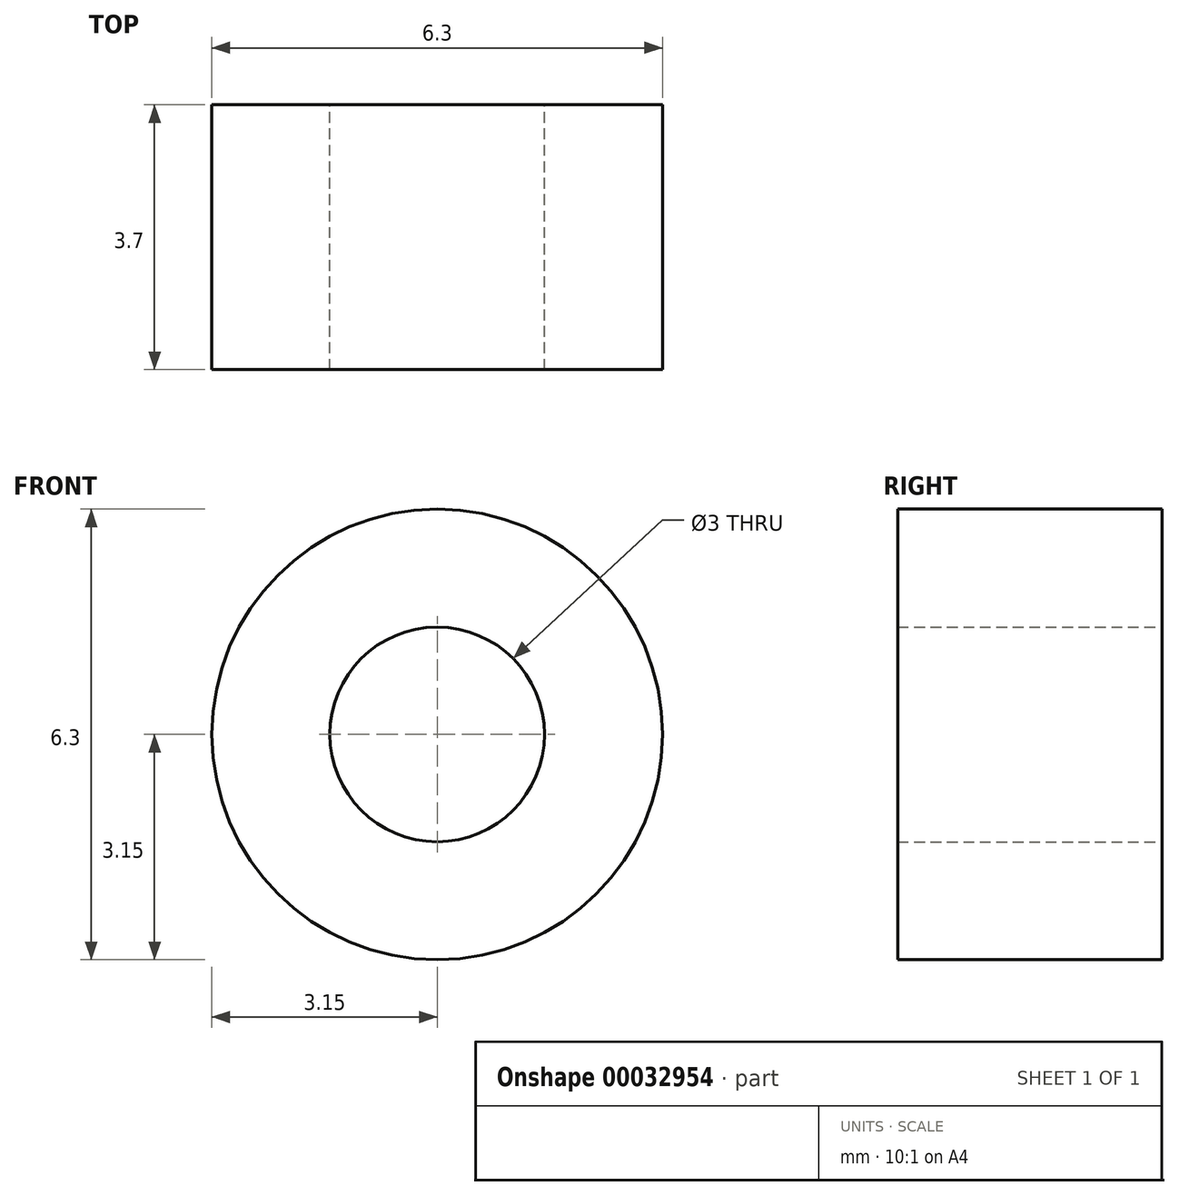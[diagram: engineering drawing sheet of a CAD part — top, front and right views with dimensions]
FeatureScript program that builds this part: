
annotation { "Feature Type Name" : "Feature", "Feature Type Description" : "" }
export const myFeature = defineFeature(function(context is Context, id is Id, definition is map)
    precondition{}
    {
        {
            var Q0;
            Q0=qCreatedBy(makeId("Front.planeOp"),FACE);
            var sketch = newSketch(context, id + "F0", { "sketchPlane" : qUnion([Q0])});
            skCircle(sketch, "E0", {"center": v(0, 0) * mm, "radius": 1.5 * mm});
            skCircle(sketch, "E1", {"center": v(0, 0) * mm, "radius": 3.15 * mm});
            skSolve(sketch);
        }
        {
            var Q0;
            Q0=qSketchRegion(id+"F0",true);
            extrude(context, id + "F1", {"entities" : qUnion([Q0]), "depth" : 3.7 * mm});
        }
    });
